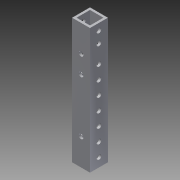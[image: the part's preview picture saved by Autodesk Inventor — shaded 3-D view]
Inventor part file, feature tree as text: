
AUTODESK INVENTOR PART (.ipt)
format: ipt  version: 2013 (Build 170138000, 138)  size: 145,920 bytes
history: native  units: in
note: dims shown in document units (in); Inventor stores cm internally (conversion verified against a paired STEP export)
features: extrude x4, sketch x4, reference x2
ambient origin geometry x8: Origin, YZ Plane, XZ Plane, XY Plane, X Axis, Y Axis, Z Axis, Center Point
bodies: Solid1 (feature_tree)
feature tree (10):
  extrude  "Extrusion1"  Depth=1.0in
  extrude  "Extrusion2"  Depth=7.0in TaperAngle=0.0deg
  extrude  "Extrusion3"  Depth=0.26in
  extrude  "Extrusion4"  Depth=4.25in
  sketch  "Sketch1"  dims[d0=1.0in d1=1.0in]
  sketch  "Sketch2"  dims[d2=0.125in d3=7.0in d4=0.0in]
  reference  "Reference5"
  reference  "Reference6"
  sketch  "Sketch3"  dims[d6=1.0in d7=0.0in d16=0.26in]
  sketch  "Sketch4"  dims[d17=0.26in d18=4.25in d19=0.26in d20=0.5in d21=0.5in d22=0.26in d23=1.0in d24=2.3622in d26=0.75in d27=0.3937in d29=1.0in d31=1.0in d32=0.0in d33=0.26in d35=1.5in d36=1.9685in d38=1.0in d39=0.3937in d41=1.0in d43=1.0in d44=0.0in]
